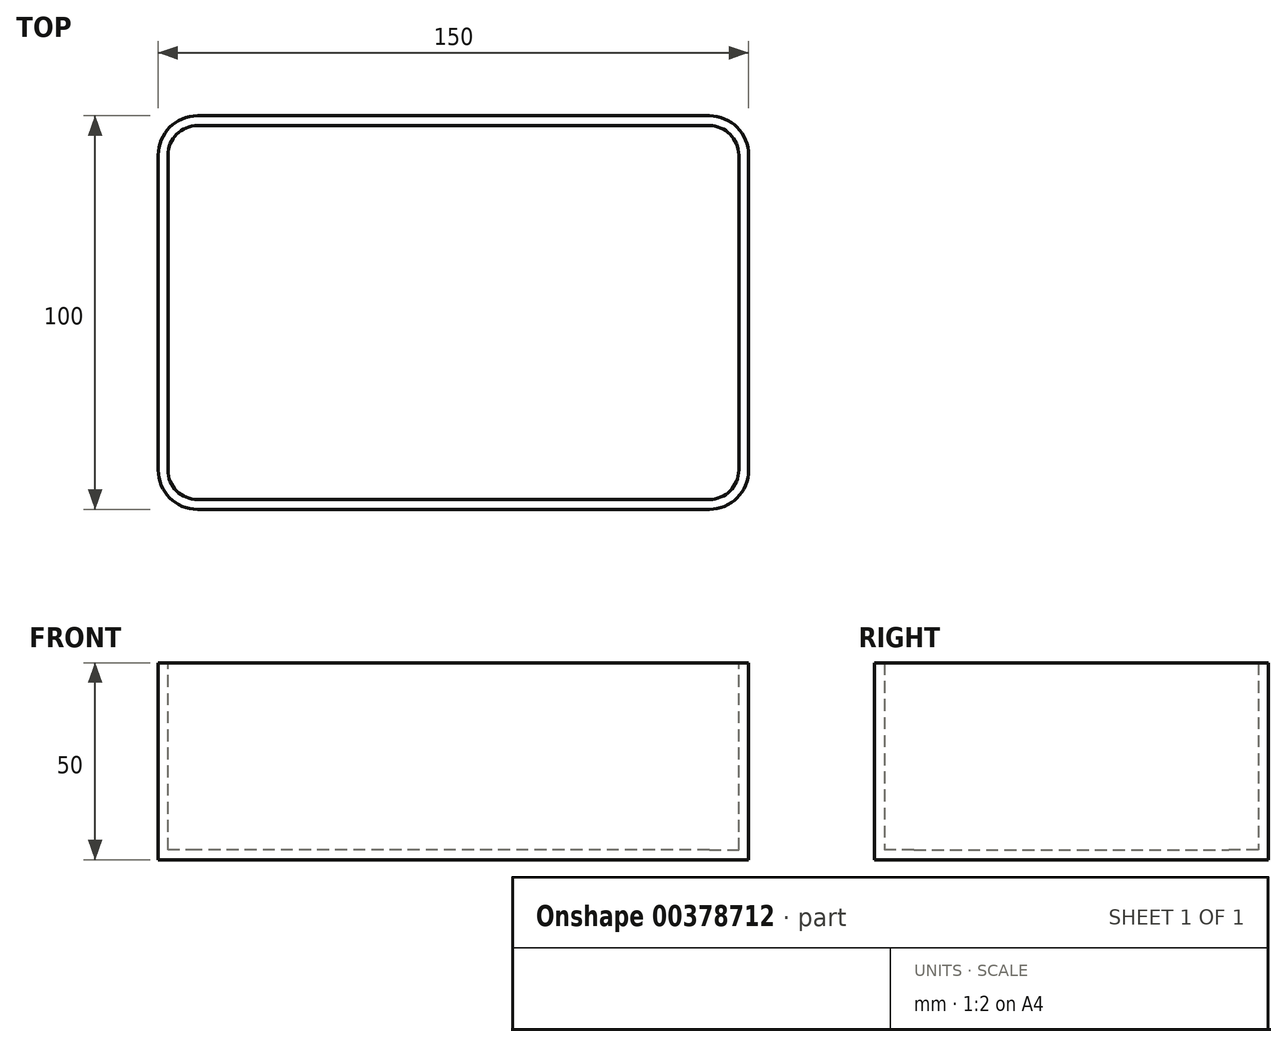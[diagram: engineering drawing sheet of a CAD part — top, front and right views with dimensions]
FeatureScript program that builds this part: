
annotation { "Feature Type Name" : "Feature", "Feature Type Description" : "" }
export const myFeature = defineFeature(function(context is Context, id is Id, definition is map)
    precondition{}
    {
        {
            var Q0;
            Q0=qCreatedBy(makeId("Top.planeOp"),FACE);
            var sketch = newSketch(context, id + "F0", { "sketchPlane" : qUnion([Q0])});
            skLineSegment(sketch, "E0.bottom", {"start": v(65, -50) * mm, "end": v(-65, -50) * mm});
            skLineSegment(sketch, "E0.top", {"start": v(65, 50) * mm, "end": v(-65, 50) * mm});
            skLineSegment(sketch, "E0.left", {"start": v(75, -40) * mm, "end": v(75, 40) * mm});
            skLineSegment(sketch, "E0.right", {"start": v(-75, -40) * mm, "end": v(-75, 40) * mm});
            skPoint(sketch, "E0.middle", {"position": v(0, 0) * mm});
            skPoint(sketch, "E1.visualSharp", {"position": v(-75, -50) * mm});
            skArc(sketch, "E1.filletArc", {"start": v(-75, -40) * mm, "mid": v(-72.07, -47.07) * mm, "end": v(-65, -50) * mm});
            skPoint(sketch, "E2.visualSharp", {"position": v(-75, 50) * mm});
            skArc(sketch, "E2.filletArc", {"start": v(-65, 50) * mm, "mid": v(-72.07, 47.07) * mm, "end": v(-75, 40) * mm});
            skPoint(sketch, "E3.visualSharp", {"position": v(75, 50) * mm});
            skArc(sketch, "E3.filletArc", {"start": v(75, 40) * mm, "mid": v(72.07, 47.07) * mm, "end": v(65, 50) * mm});
            skPoint(sketch, "E4.visualSharp", {"position": v(75, -50) * mm});
            skArc(sketch, "E4.filletArc", {"start": v(65, -50) * mm, "mid": v(72.07, -47.07) * mm, "end": v(75, -40) * mm});
            skSolve(sketch);
        }
        {
            var Q0;
            Q0 = qSketchRegion(id + "F0", true);
            extrude(context, id + "F1", {"entities" : qUnion([Q0]), "depth" : 50 * mm});
        }
        {
            var Q0;
            Q0=makeQuery(id+"F1.opExtrude","CAP_FACE",FACE,{"disambiguationData":[OSD([sQuery(id+"F0.wireOp",EDGE,"E0.bottom"),sQuery(id+"F0.wireOp",EDGE,"E0.top"),sQuery(id+"F0.wireOp",EDGE,"E0.left"),sQuery(id+"F0.wireOp",EDGE,"E0.right")])],"isStart":false});
            shell(context, id + "F2", {"entities" : qUnion([Q0]), "thickness" : 2.5 * mm});
        }
    });
